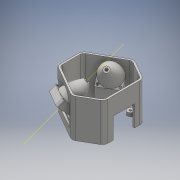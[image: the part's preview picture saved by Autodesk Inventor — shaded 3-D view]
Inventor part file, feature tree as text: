
AUTODESK INVENTOR PART (.ipt)
format: ipt  version: 2016 SP1 (Build 200210100, 210)  size: 582,144 bytes
history: native  units: mm
features: sketch x14, extrude x13, projected_geometry x5, reference x4, plane x3, revolve x1, mirror x1, fillet x1, other x1
ambient origin geometry x8: Origin, YZ Plane, XZ Plane, XY Plane, X Axis, Y Axis, Z Axis, Center Point
bodies: Solid1 (feature_tree)
feature tree (43):
  extrude  "Extrusion1"  Depth=2.0mm
  plane  "Work Plane1"
  sketch  "Sketch3"  dims[d4=0.5mm d7=0.5mm]
  plane  "Work Plane2"
  plane  "Work Plane3"
  revolve  "Revolution2"  [1 undecoded]
  extrude  "Extrusion4"  Depth=1.5mm
  extrude  "Extrusion5"  Depth=10.0mm TaperAngle=0.0deg
  extrude  "Extrusion6"  Depth=10.0mm TaperAngle=0.0deg
  extrude  "Extrusion7"  Depth=10.0mm TaperAngle=0.0deg
  extrude  "Extrusion8"  Depth=45.0mm TaperAngle=0.0deg
  extrude  "Extrusion10"  Depth=45.0mm TaperAngle=0.0deg
  extrude  "Extrusion11"  Depth=16.0mm TaperAngle=0.0deg
  extrude  "Extrusion12"  Depth=9.0mm
  extrude  "Extrusion14"  Depth=3.0mm
  extrude  "Extrusion15"  Depth=5.0mm TaperAngle=0.0deg
  mirror  "Mirror2"
  extrude  "Extrusion16"  [1 undecoded]
  extrude  "Extrusion17"  [1 undecoded]
  fillet  "Fillet1"  [1 undecoded]
  sketch  "Sketch1"  dims[d0=2.0mm d3=0.5mm]
  reference  "Reference1"
  reference  "Reference2"
  reference  "Reference3"
  reference  "Reference4"
  other  "Work Axis1"
  sketch  "Sketch5"  dims[d8=10.0mm d9=0.0mm d13=1.5mm]
  sketch  "Sketch7"  dims[d14=90.0deg d19=10.0mm d20=0.0mm]
  sketch  "Sketch8"  dims[d21=10.0mm d22=0.0mm d23=10.0mm d24=0.0mm]
  projected_geometry  "Projected Loop3"
  sketch  "Sketch9"  dims[d25=10.0mm d26=0.0mm d27=10.0mm d28=0.0mm]
  sketch  "Sketch10"  dims[d31=45.0mm d32=0.0mm d33=45.0mm d34=0.0mm]
  projected_geometry  "Projected Loop4"
  projected_geometry  "Projected Loop5"
  sketch  "Sketch11"  dims[d35=45.0mm d36=0.0mm d39=0.1mm d40=0.0mm]
  sketch  "Sketch12"  dims[d41=25.0mm d42=16.0mm d43=0.0mm]
  sketch  "Sketch14"  dims[d44=10.0mm d45=0.0mm d46=9.0mm]
  projected_geometry  "Projected Loop9"
  sketch  "Sketch16"  dims[d47=6.0mm d48=3.0mm]
  projected_geometry  "Projected Loop11"
  sketch  "Sketch17"  dims[d49=30.0mm d51=360.0deg d53=5.0mm d54=0.0mm]
  sketch  "Sketch18"  dims[d55=2.0mm]
  sketch  "Sketch19"
note: 4 required parameter values undecoded (feature->parameter linkage not recoverable at this tier; creation-order binding heuristic only, values carry confidence <= 0.55)